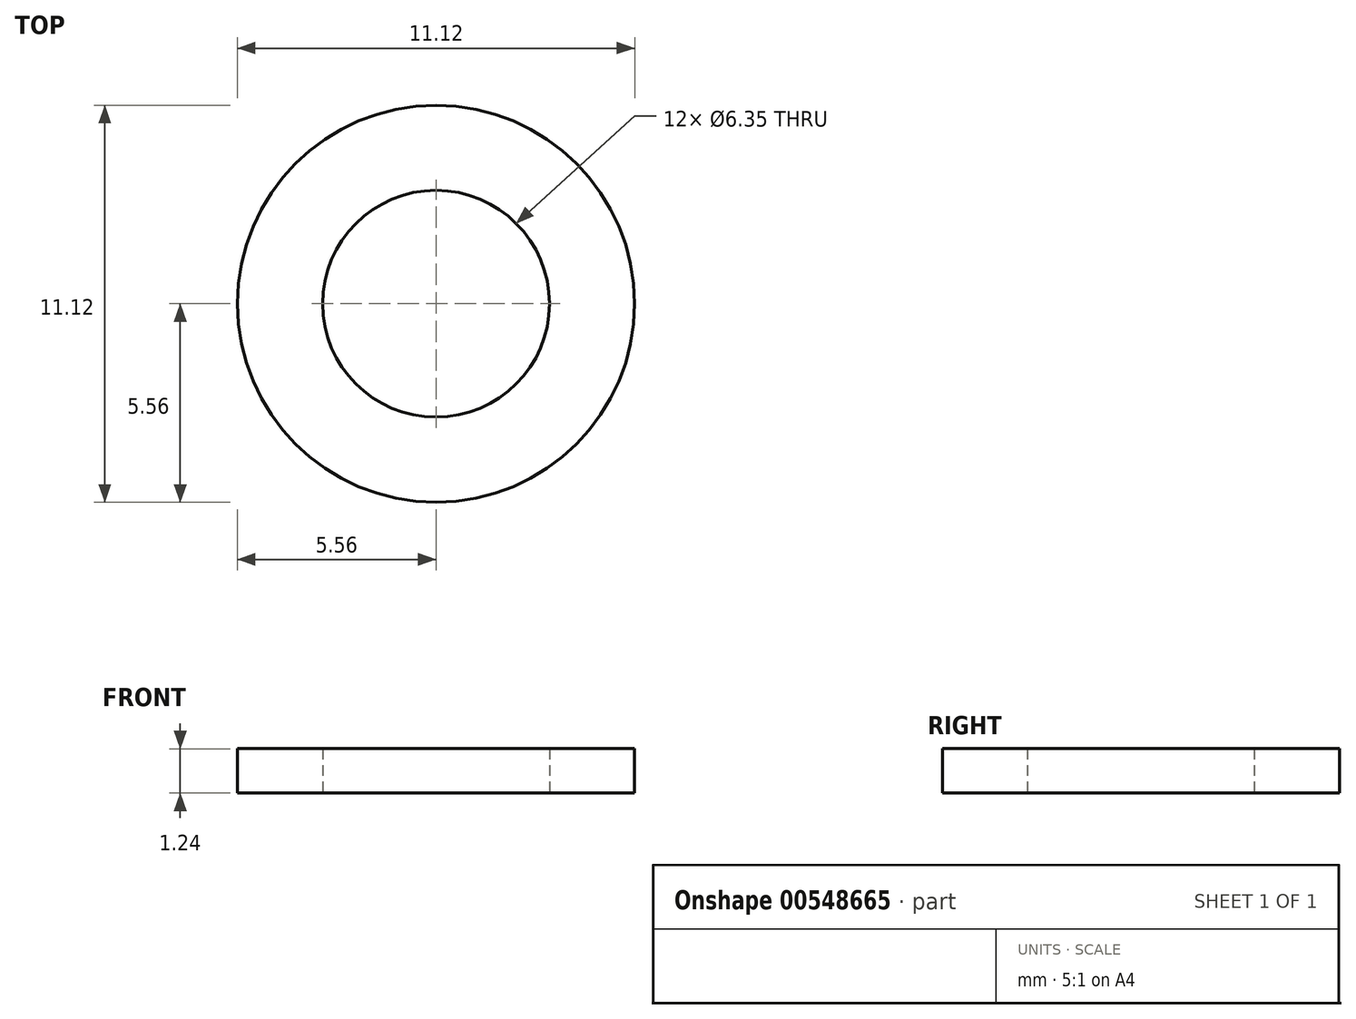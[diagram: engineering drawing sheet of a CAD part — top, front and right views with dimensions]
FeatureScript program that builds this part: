
annotation { "Feature Type Name" : "Feature", "Feature Type Description" : "" }
export const myFeature = defineFeature(function(context is Context, id is Id, definition is map)
    precondition{}
    {
        {
            var Q0;
            Q0=qCreatedBy(makeId("Top.planeOp"),FACE);
            var sketch = newSketch(context, id + "F0", { "sketchPlane" : qUnion([Q0])});
            skCircle(sketch, "E0", {"center": v(0, 0) * mm, "radius": 5.56 * mm});
            skCircle(sketch, "E1", {"center": v(0, 0) * mm, "radius": 3.18 * mm});
            skSolve(sketch);
        }
        {
            var Q0;
            Q0=makeQuery(id+"F0.imprint","IMPRINT",FACE,{"disambiguationData":[TD([[makeQuery(id+"F0.imprint","IMPRINT",EDGE,{"derivedFrom":sQuery(id+"F0.wireOp",EDGE,"E0")}),1.0]])]});
            extrude(context, id + "F1", {"entities" : qUnion([Q0]), "endBound" : BoundingType.SYMMETRIC, "depth" : 1.24 * mm, "offsetDistance" : 25.4 * mm});
        }
    });
